# Revit family: Indoor 180 types Avec hôte DD
name_source: partatom
category: Dispositifs d'éclairage
units: mm (PartAtom-declared; Revit-internal decimal feet)

## family parameters
Conserver l'orientation des annotations = Oui
Cote de connecteur circulaire = Utiliser le diamètre
Couper avec des vides une fois chargée = Non
Hôte = Face
Partagée = Non
Point de calcul de pièce = Non
Type d'élément = Normal

## types (17) — shared parameters
Classe = II
Code d'assemblage = D5010200
Elévation par défaut = 110 cm
Fabricant = B.E.G.
Hauteur de montage max = 220 cm
IP = 20
Image du type = MURAL.jpg
Marque = LUXOMAT
Position en hauteur = 110 cm
URL = http://www.luxomat.com

## per-type parameters (varying)
| type | Alimentation | Charge Cos ɸ =0.5 | Charge Cos ɸ =1 | Charge LED | Commentaires du type | Consommation | Mode de pose | Modèle | Relais | Référence | Température ambiante | Type de Sortie |
| 01- INDOOR 180-EN Générique | 110-240 V AC |  |  |  | INTER.AUTO.180°/10M ENCASTRE MURAL |  | Encastré mural | INDOOR 180-EN |  |  | -25°C à +50°C |  |
| 02- INDOOR 180-R-EN réf 92623 | 110-240 V AC | 1150 VA | 2300 W | 300 W | INTER.AUTO.3 FILS.1 CONTACT.180°/10M ENCASTRE MURAL | 1.3 W | Encastré mural | INDOOR 180-R-EN | 10 A | 92623 | -25°C à +50°C | TOR - Version 3 Fils |
| 03- INDOOR 180-T-EN réf 92622 | 110-240 V AC | 0 | 40 W min à 300 W maxi | 0 | INTER.AUTO.2 FILS.1 CONTACT.180°/10M ENCASTRE MURAL | 1.3 W | Encastré mural | INDOOR 180-T-EN | 1.3 A | 92622 | -25°C à +50°C | TOR - Version 2 Fils |
| 16- INDOOR 180-R-11-48V-3A-EN réf 92621 | 11-48 V AC/DC | 0 | 0 | 0 | INTER.AUTO.11-48V.1 CONTACT.3A.180°/10M ENCASTRE MURAL | 1 W | Encastré mural | INDOOR 180-R-11-48V-3A-EN | 3 A | 92621 | -25°C à +50°C | TOR |
| 17- INDOOR 180-R-11-48V-RR-EN réf 92667 | 11-48 V AC/DC | 0 | 0 | 0 | INTER.AUTO.11-48V.1 CONTACT.RR.180°/10M ENCASTRE MURAL - CADRE NON INCLUS | 1 W | Encastré mural | INDOOR 180-R-11-48V-RR-EN | 100 mA | 92667 | -25°C à +50°C | Reed Relais |
| 04- INDOOR 180-SC-EN réf 92650 | 110-240 V AC | 0 | 0 | 0 | INTER.AUTO.2 FILS.1 CONTACT.REMPLACEMENT BP.180°/10M ENCASTRE MURAL | 0.8 W | Encastré mural | INDOOR 180-SC-EN | 200 mA | 92650 | -25°C à +50°C | TOR - Version 2 Fils en remplacement de BP sur minuterie |
| 05- INDOOR 180-M-2C-EN réf 92136 | 110-240 V AC | 1150 VA | 2300 W | 300 W | INTER.AUTO.MAITRE.2 CONTACTS.180°/10M ENCASTRE MURAL | 0.4 W | -25°C à +50°C | INDOOR 180-M-2C-EN | 10 A / 3A | 92136 | -25°C à +50°C | TOR + CVC |
| 10- INDOOR 180-KNX-BA-EN réf 93362 | 24 V DC par bus KNX | 0 | 0 | 0 | INTER.AUTO.KNX.VERSION BASIQUE.180°/10M ENCASTRE MURAL | 12 mA | Encastré mural | INDOOR 180-KNX-BA-EN | 0 | 93362 | -5°C à +45°C | KNX - 1 sortie Eclairage TOR |
| 11- INDOOR 180-KNX-ST-EN réf 93363 | 24 V DC par bus KNX | 0 | 0 | 0 | INTER.AUTO.KNX.VERSION STANDARD.180°/10M ENCASTRE MURAL | 12 mA | Encastré mural | INDOOR 180-KNX-ST-EN | 0 | 93363 | -5°C à +45°C | KNX - 1 sortie Eclairage TOR ou GRADATION / 3 sorties Présence |
| 12- INDOOR 180-KNX-DX-EN réf 93364 | 24 V DC par bus KNX | 0 | 0 | 0 | INTER.AUTO.KNX.VERSION DELUXE.180°/10M ENCASTRE MURAL | 12 mA | Encastré mural | INDOOR 180-KNX-DX-EN | 0 | 93364 | -5°C à +45°C | KNX - 1 sortie Eclairage TOR ou GRADATION / 3 sorties Présence / Capteur de température et bruit |
| 15- INDOOR 180-LON-EN réf 92329 | 24 V DC par BUS LON | 0 | 0 | 0 | INTER.AUTO.LON.180°/10M ENCASTRE MURAL | 12 mA | Encastré mural | INDOOR 180-LON-EN | 0 | 92329 | -5°C à +45°C | LON |
| 06- INDOOR 180-S-EN réf 92135 | 110-240 V AC | 0 | 0 | 0 | INTER.AUTO.ESCLAVE.180°/10M ENCASTRE MURAL | 0.25 W | Encastré mural | INDOOR 180-S-EN | 0 | 92135 | -25°C à +50°C | Esclave |
| 07- INDOOR 180-DALILINK-EN réf 93848 | 16V DC par bus DALI | 0 | 0 | 0 | MULTI.CAPTEUR.PRES.DALILINK.180°/10M ENCASTRE MURAL | 7 mA | Encastré mural | INDOOR 180-DALILINK-EN | 0 | 93848 | -25°C à +55°C | DALILINK |
| 08- INDOOR 180-DALISYS-EN réf 93326 | 10-22V DC par bus DALI | 0 | 0 | 0 | MULTI.CAPTEUR.PRES.DALISYS.180°/10M ENCASTRE MURAL | 7 mA | Encastré mural | INDOOR 180-DALISYS-EN | 0 | 93326 | -25°C à +55°C | DALI Adressable |
| 09- INDOOR 180-BMS-DALI-2-EN réf 93540 | 10-22V DC par bus DALI | 0 | 0 | 0 | MULTI.CAPTEUR.PRES.BMS.DALI 2.180°/10M ENCASTRE MURAL | 7 mA | Encastré mural | INDOOR 180-BMS-DALI-2-EN | 0 | 93540 | -25°C à +55°C | DALI 2 Adressable - BMS |
| 13- INDOOR 180-KNXs-ST-EN réf 93524 | 24 V DC par bus KNX | 0 | 0 | 0 | INTER.AUTO.KNX Sécure.VERSION STANDARD.180°/10M ENCASTRE MURAL | 12 mA | Encastré mural | INDOOR 180-KNXs-ST-EN | 0 | 93524 | -5°C à +45°C | KNX Sécure - 1 sortie Eclairage TOR ou GRADATION / 3 sorties Présence / HCL |
| 14- INDOOR 180-KNXs-DX-EN réf 93525 | 24 V DC par bus KNX | 0 | 0 | 0 | INTER.AUTO.KNX Sécure.VERSION DELUXE.180°/10M ENCASTRE MURAL | 12 mA | Encastré mural | INDOOR 180-KNXs-DX-EN | 0 | 93525 | -5°C à +45°C | KNX Sécure - 1 sortie Eclairage TOR ou GRADATION / 3 sorties Présence / Capteur de température et bruit / HCL |
